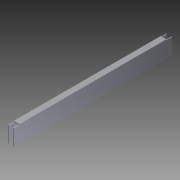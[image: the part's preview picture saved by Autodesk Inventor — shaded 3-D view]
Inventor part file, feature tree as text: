
AUTODESK INVENTOR PART (.ipt)
format: ipt  version: 2012 (Build 160160000, 160)  size: 105,984 bytes
history: native  units: in
note: dims shown in document units (in); Inventor stores cm internally (conversion verified against a paired STEP export)
features: extrude x3, sketch x3
ambient origin geometry x8: Origin, YZ Plane, XZ Plane, XY Plane, X Axis, Y Axis, Z Axis, Center Point
bodies: Solid1 (feature_tree)
feature tree (6):
  extrude  "Extrusion1"  Depth=3.0in
  extrude  "Extrusion2"  Depth=0.125in
  extrude  "Extrusion3"  Depth=0.125in
  sketch  "Sketch1"  dims[d0=1.0in d1=3.0in]
  sketch  "Sketch2"  dims[d2=0.125in d3=0.125in]
  sketch  "Sketch3"  dims[d4=0.125in d5=0.125in d6=27.75in d7=0.0in d8=1.0in d9=1.0in d10=0.125in d11=0.0in d12=1.0in d13=1.0in d14=0.125in d15=0.0in]
